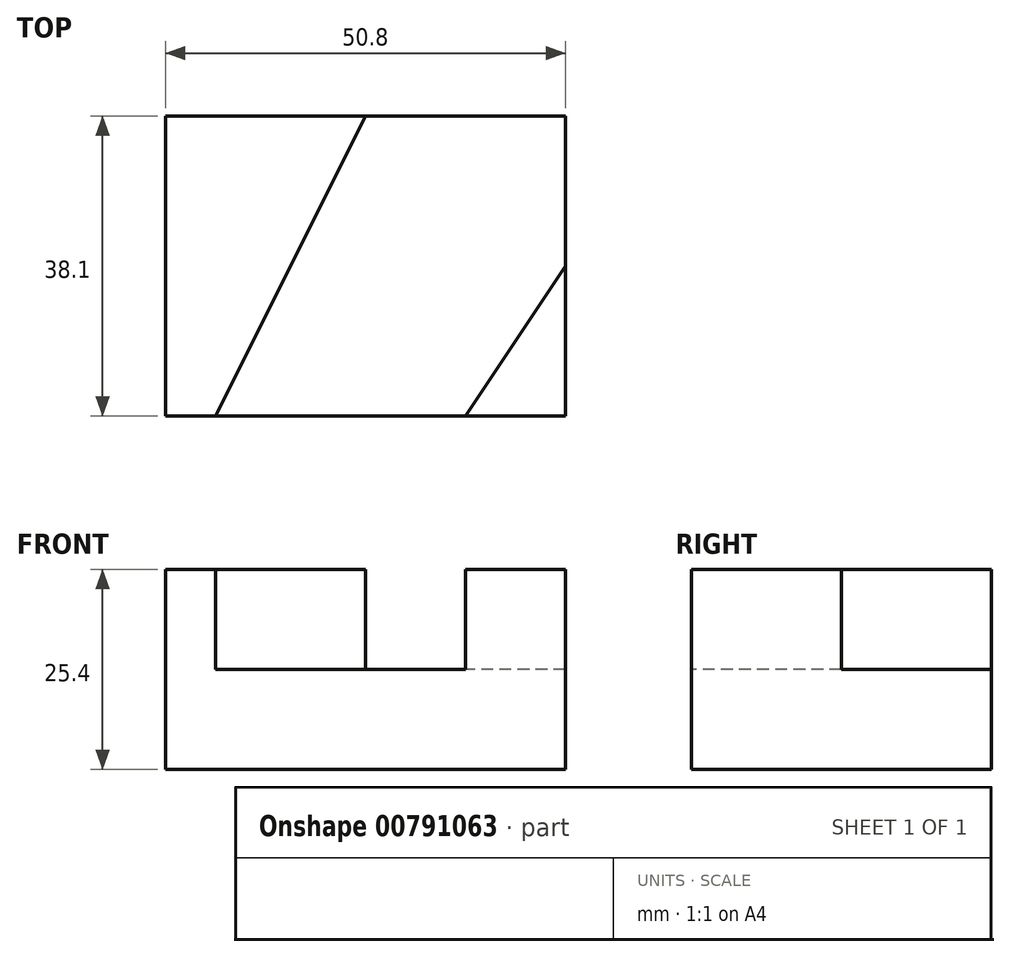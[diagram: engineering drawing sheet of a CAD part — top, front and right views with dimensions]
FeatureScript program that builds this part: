
annotation { "Feature Type Name" : "Feature", "Feature Type Description" : "" }
export const myFeature = defineFeature(function(context is Context, id is Id, definition is map)
    precondition{}
    {
        {
            var Q0;
            Q0=qCreatedBy(makeId("Front.planeOp"),FACE);
            var sketch = newSketch(context, id + "F0", { "sketchPlane" : qUnion([Q0])});
            skLineSegment(sketch, "E0", {"start": v(0, 0) * mm, "end": v(50.8, 0) * mm});
            skLineSegment(sketch, "E1", {"start": v(50.8, 0) * mm, "end": v(50.8, 25.4) * mm});
            skLineSegment(sketch, "E2", {"start": v(50.8, 25.4) * mm, "end": v(0, 25.4) * mm});
            skLineSegment(sketch, "E3", {"start": v(0, 25.4) * mm, "end": v(0, 0) * mm});
            skSolve(sketch);
        }
        {
            var Q0;
            Q0=qSketchRegion(id+"F0",true);
            extrude(context, id + "F1", {"entities" : qUnion([Q0]), "depth" : 38.1 * mm, "offsetDistance" : 25.4 * mm});
        }
        {
            var Q0;
            Q0=makeQuery(id+"F1.opExtrude","SWEPT_FACE",FACE,{"disambiguationData":[OSD([sQuery(id+"F0.wireOp",EDGE,"E2")])]});
            var sketch = newSketch(context, id + "F2", { "sketchPlane" : qUnion([Q0])});
            skLineSegment(sketch, "E4", {"start": v(50.8, -38.1) * mm, "end": v(38.1, -38.1) * mm});
            skLineSegment(sketch, "E5", {"start": v(50.8, -38.1) * mm, "end": v(50.8, -19.05) * mm});
            skLineSegment(sketch, "E6", {"start": v(50.8, -19.05) * mm, "end": v(38.1, -38.1) * mm});
            skLineSegment(sketch, "E7", {"start": v(0, 0) * mm, "end": v(25.4, 0) * mm});
            skLineSegment(sketch, "E8", {"start": v(0, -38.1) * mm, "end": v(6.35, -38.1) * mm});
            skLineSegment(sketch, "E9", {"start": v(6.35, -38.1) * mm, "end": v(25.4, 0) * mm});
            skSolve(sketch);
        }
        {
            var Q0;
            {var subQ5=sQuery(id+"F2.wireOp",EDGE,"E6");Q0=makeQuery(id+"F2.imprint","IMPRINT",FACE,{"disambiguationData":[TD([[makeQuery(id+"F2.imprint","IMPRINT",EDGE,{"derivedFrom":subQ5}),-1.0]])]});}
            extrude(context, id + "F3", {"entities" : qUnion([Q0]), "operationType" : NewBodyOperationType.REMOVE, "oppositeDirection" : true, "depth" : 12.7 * mm, "offsetDistance" : 25.4 * mm});
        }
    });
